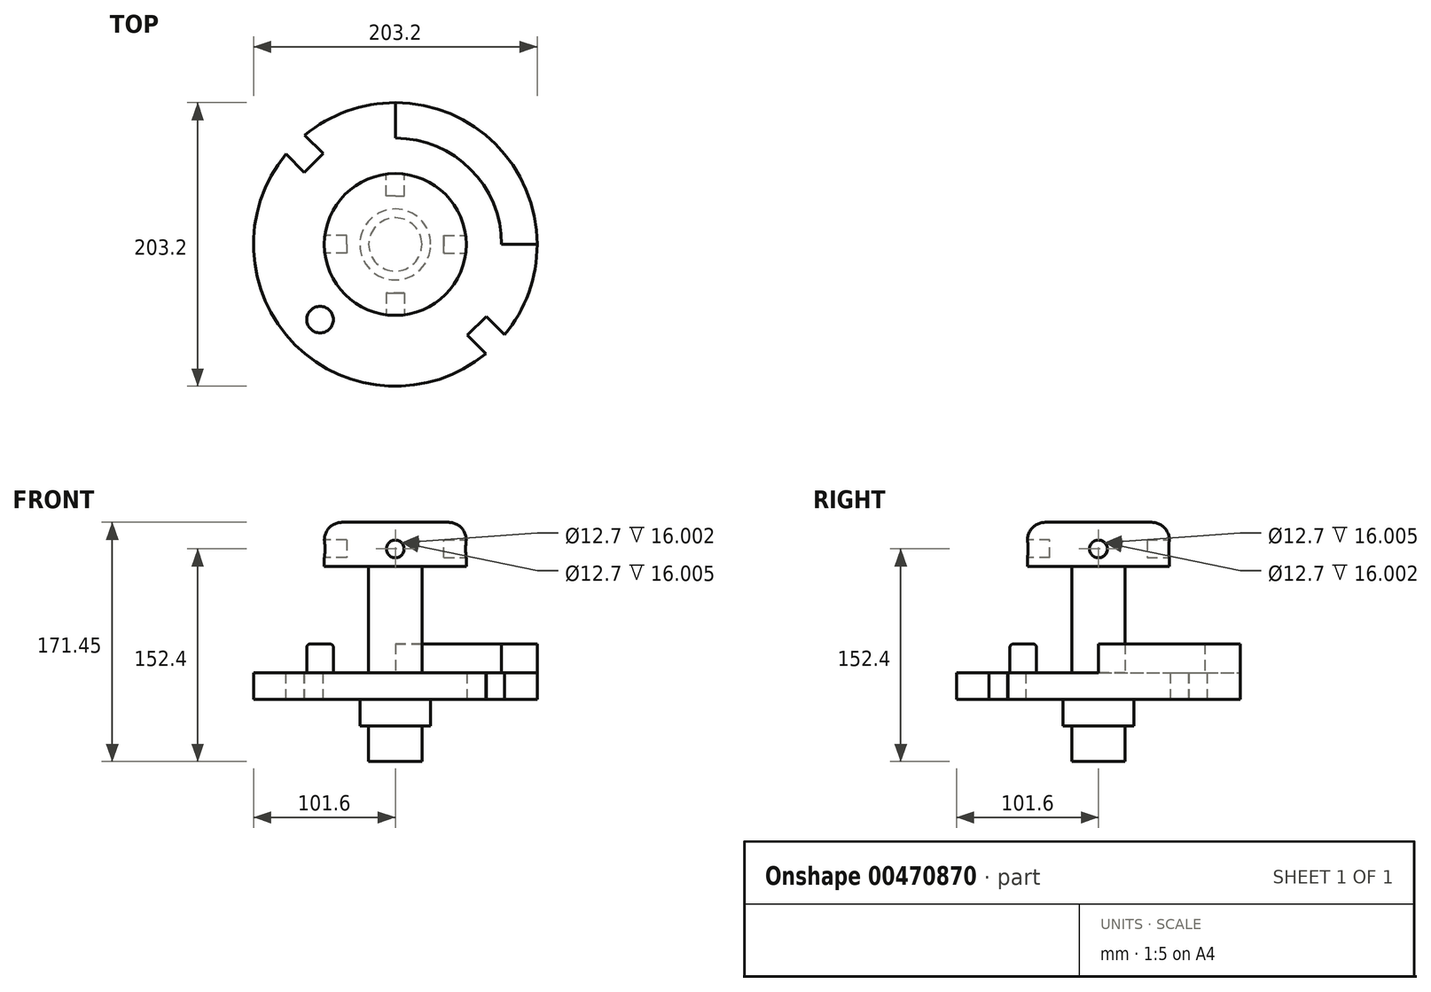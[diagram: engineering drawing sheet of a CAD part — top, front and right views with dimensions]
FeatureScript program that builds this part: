
annotation { "Feature Type Name" : "Feature", "Feature Type Description" : "" }
export const myFeature = defineFeature(function(context is Context, id is Id, definition is map)
    precondition{}
    {
        {
            var Q0;
            Q0=qCreatedBy(makeId("Top.planeOp"),FACE);
            var sketch = newSketch(context, id + "F0", { "sketchPlane" : qUnion([Q0])});
            skCircle(sketch, "E0", {"center": v(0, 0) * mm, "radius": 19.05 * mm});
            skSolve(sketch);
        }
        {
            var Q0;
            Q0=makeQuery(id+"F0.imprint","IMPRINT",FACE,{"disambiguationData":[TD([[makeQuery(id+"F0.imprint","IMPRINT",EDGE,{"derivedFrom":sQuery(id+"F0.wireOp",EDGE,"E0")}),1.0]])]});
            extrude(context, id + "F1", {"entities" : qUnion([Q0]), "depth" : 76.2 * mm});
        }
        {
            var Q0;
            Q0=makeQuery(id+"F1.opExtrude","CAP_FACE",FACE,{"disambiguationData":[OSD([sQuery(id+"F0.wireOp",EDGE,"E0")])],"isStart":false});
            var sketch = newSketch(context, id + "F2", { "sketchPlane" : qUnion([Q0])});
            skCircle(sketch, "E1", {"center": v(0, 0) * mm, "radius": 50.8 * mm});
            skSolve(sketch);
        }
        {
            var Q0;
            Q0=makeQuery(id+"F2.imprint","IMPRINT",FACE,{"disambiguationData":[TD([[makeQuery(id+"F2.imprint","IMPRINT",EDGE,{"derivedFrom":sQuery(id+"F2.wireOp",EDGE,"E1")}),1.0]])]});
            var Q1;
            Q1=makeQuery(id+"F2.imprint","IMPRINT",FACE,{"disambiguationData":[TD([[makeQuery(id+"F2.imprint","IMPRINT",EDGE,{"derivedFrom":makeQuery(id+"F1.opExtrude","CAP_EDGE",EDGE,{"disambiguationData":[OSD([sQuery(id+"F0.wireOp",EDGE,"E0")])],"isStart":false})}),1.0]])]});
            extrude(context, id + "F3", {"entities" : qUnion([Q0, Q1]), "operationType" : NewBodyOperationType.ADD, "depth" : 31.75 * mm});
        }
        {
            var Q0;
            Q0=makeQuery(id+"F3.opExtrude","CAP_EDGE",EDGE,{"disambiguationData":[OSD([sQuery(id+"F2.wireOp",EDGE,"E1")])],"isStart":false});
            fillet(context, id + "F4", {"entities" : qUnion([Q0]), "radius" : 12.7 * mm, "tangentPropagation" : true, "allowEdgeOverflow" : false});
        }
        {
            var Q0;
            Q0=qCreatedBy(makeId("Front.planeOp"),FACE);
            cPlane(context, id + "F5", {"entities" : qUnion([Q0]), "cplaneType" : CPlaneType.OFFSET, "offset" : 50.8 * mm, "width" : 152.4 * mm, "height" : 152.4 * mm});
        }
        {
            var Q0;
            Q0=qCreatedBy(id+"F5.planeOp",FACE);
            var sketch = newSketch(context, id + "F6", { "sketchPlane" : qUnion([Q0])});
            skLineSegment(sketch, "E2", {"start": v(0, 0) * mm, "end": v(0, 88.9) * mm});
            skCircle(sketch, "E3", {"center": v(0, 88.9) * mm, "radius": 6.35 * mm});
            skSolve(sketch);
        }
        {
            var Q0;
            Q0=makeQuery(id+"F6.imprint","IMPRINT",FACE,{"disambiguationData":[TD([[makeQuery(id+"F6.imprint","IMPRINT",EDGE,{"derivedFrom":sQuery(id+"F6.wireOp",EDGE,"E3")}),1.0]])]});
            extrude(context, id + "F7", {"entities" : qUnion([Q0]), "operationType" : NewBodyOperationType.REMOVE, "oppositeDirection" : true, "depth" : 16 * mm});
        }
        {
            var Q0;
            Q0=qCreatedBy(makeId("Right.planeOp"),FACE);
            cPlane(context, id + "F8", {"entities" : qUnion([Q0]), "cplaneType" : CPlaneType.OFFSET, "offset" : 50.8 * mm, "oppositeDirection" : true, "width" : 152.4 * mm, "height" : 152.4 * mm});
        }
        {
            var Q0;
            Q0=qCreatedBy(id+"F8.planeOp",FACE);
            var sketch = newSketch(context, id + "F9", { "sketchPlane" : qUnion([Q0])});
            skLineSegment(sketch, "E4", {"start": v(0, 0) * mm, "end": v(0, 88.9) * mm});
            skCircle(sketch, "E5", {"center": v(0, 88.9) * mm, "radius": 6.35 * mm});
            skSolve(sketch);
        }
        {
            var Q0;
            Q0=makeQuery(id+"F9.imprint","IMPRINT",FACE,{"disambiguationData":[TD([[makeQuery(id+"F9.imprint","IMPRINT",EDGE,{"derivedFrom":sQuery(id+"F9.wireOp",EDGE,"E5")}),1.0]])]});
            extrude(context, id + "F10", {"entities" : qUnion([Q0]), "operationType" : NewBodyOperationType.REMOVE, "depth" : 16 * mm});
        }
        {
            var Q0;
            Q0=qCreatedBy(makeId("Front.planeOp"),FACE);
            cPlane(context, id + "F11", {"entities" : qUnion([Q0]), "cplaneType" : CPlaneType.OFFSET, "offset" : 50.8 * mm, "oppositeDirection" : true, "width" : 152.4 * mm, "height" : 152.4 * mm});
        }
        {
            var Q0;
            Q0=qCreatedBy(id+"F11.planeOp",FACE);
            var sketch = newSketch(context, id + "F12", { "sketchPlane" : qUnion([Q0])});
            skLineSegment(sketch, "E6", {"start": v(0, 0) * mm, "end": v(0, 88.9) * mm});
            skCircle(sketch, "E7", {"center": v(0, 88.9) * mm, "radius": 6.35 * mm});
            skSolve(sketch);
        }
        {
            var Q0;
            Q0=makeQuery(id+"F12.imprint","IMPRINT",FACE,{"disambiguationData":[TD([[makeQuery(id+"F12.imprint","IMPRINT",EDGE,{"derivedFrom":sQuery(id+"F12.wireOp",EDGE,"E7")}),1.0]])]});
            extrude(context, id + "F13", {"entities" : qUnion([Q0]), "operationType" : NewBodyOperationType.REMOVE, "depth" : 16 * mm});
        }
        {
            var Q0;
            Q0=qCreatedBy(makeId("Right.planeOp"),FACE);
            cPlane(context, id + "F14", {"entities" : qUnion([Q0]), "cplaneType" : CPlaneType.OFFSET, "offset" : 50.8 * mm, "width" : 152.4 * mm, "height" : 152.4 * mm});
        }
        {
            var Q0;
            Q0=qCreatedBy(id+"F14.planeOp",FACE);
            var sketch = newSketch(context, id + "F15", { "sketchPlane" : qUnion([Q0])});
            skLineSegment(sketch, "E8", {"start": v(0, 0) * mm, "end": v(0, 88.9) * mm});
            skCircle(sketch, "E9", {"center": v(0, 88.9) * mm, "radius": 6.35 * mm});
            skSolve(sketch);
        }
        {
            var Q0;
            Q0=makeQuery(id+"F15.imprint","IMPRINT",FACE,{"disambiguationData":[TD([[makeQuery(id+"F15.imprint","IMPRINT",EDGE,{"derivedFrom":sQuery(id+"F15.wireOp",EDGE,"E9")}),1.0]])]});
            extrude(context, id + "F16", {"entities" : qUnion([Q0]), "operationType" : NewBodyOperationType.REMOVE, "oppositeDirection" : true, "depth" : 16 * mm});
        }
        {
            var Q0;
            Q0=makeQuery(id+"F1.opExtrude","CAP_FACE",FACE,{"disambiguationData":[OSD([sQuery(id+"F0.wireOp",EDGE,"E0")])],"isStart":true});
            var sketch = newSketch(context, id + "F17", { "sketchPlane" : qUnion([Q0])});
            skCircle(sketch, "E10", {"center": v(0, 0) * mm, "radius": 101.6 * mm});
            skLineSegment(sketch, "E11", {"start": v(0, 0) * mm, "end": v(101.6, 0) * mm});
            skLineSegment(sketch, "E12", {"start": v(0, 0) * mm, "end": v(0, 101.6) * mm});
            skLineSegment(sketch, "E13", {"start": v(0, 101.6) * mm, "end": v(101.6, 101.6) * mm});
            skLineSegment(sketch, "E14", {"start": v(101.6, 101.6) * mm, "end": v(101.6, 0) * mm});
            skLineSegment(sketch, "E15", {"start": v(0, 0) * mm, "end": v(101.6, 101.6) * mm});
            skLineSegment(sketch, "E16.0", {"start": v(32.14, 18.66) * mm, "end": v(108.34, 94.86) * mm});
            skLineSegment(sketch, "E17.0", {"start": v(18.66, 32.14) * mm, "end": v(94.86, 108.34) * mm});
            skLineSegment(sketch, "E18", {"start": v(71.84, 71.84) * mm, "end": v(58.37, 58.37) * mm});
            skLineSegment(sketch, "E19", {"start": v(58.37, 58.37) * mm, "end": v(51.64, 65.1) * mm});
            skLineSegment(sketch, "E20", {"start": v(58.37, 58.37) * mm, "end": v(65.1, 51.64) * mm});
            skLineSegment(sketch, "E21", {"start": v(0, 0) * mm, "end": v(-101.6, 0) * mm});
            skLineSegment(sketch, "E22", {"start": v(0, 101.6) * mm, "end": v(-101.6, 101.6) * mm});
            skLineSegment(sketch, "E23", {"start": v(-101.6, 101.6) * mm, "end": v(-101.6, 0) * mm});
            skLineSegment(sketch, "E24", {"start": v(0, 0) * mm, "end": v(-101.6, 101.6) * mm});
            skLineSegment(sketch, "E25.MirrorCS", {"start": v(-58.37, -58.37) * mm, "end": v(-65.1, -51.64) * mm});
            skLineSegment(sketch, "E26.MirrorCS", {"start": v(-58.37, -58.37) * mm, "end": v(-51.64, -65.1) * mm});
            skLineSegment(sketch, "E27.MirrorCS", {"start": v(-32.14, -18.66) * mm, "end": v(-108.34, -94.86) * mm});
            skLineSegment(sketch, "E28.MirrorCS", {"start": v(-18.66, -32.14) * mm, "end": v(-94.86, -108.34) * mm});
            skSolve(sketch);
        }
        {
            var Q0;
            {var subQ0=sQuery(id+"F17.wireOp",EDGE,"E19");Q0=makeQuery(id+"F17.imprint","IMPRINT",FACE,{"disambiguationData":[TD([[makeQuery(id+"F17.imprint","IMPRINT",EDGE,{"derivedFrom":subQ0}),1.0]])]});}
            var Q1;
            {var subQ1=sQuery(id+"F17.wireOp",EDGE,"E10");var subQ3=sQuery(id+"F17.wireOp",EDGE,"E24");var subQ4=makeQuery(id+"F17.imprint","INTERSECT",VERTEX,{"derivedFrom":[subQ1,subQ3]});Q1=makeQuery(id+"F17.imprint","IMPRINT",FACE,{"disambiguationData":[TD([[makeQuery(id+"F17.imprint","IMPRINT",EDGE,{"disambiguationData":[TD([[subQ4,1.0]])],"derivedFrom":subQ3}),-1.0]])]});}
            var Q2;
            {var subQ1=sQuery(id+"F17.wireOp",EDGE,"E10");var subQ3=sQuery(id+"F17.wireOp",EDGE,"E24");var subQ4=makeQuery(id+"F17.imprint","INTERSECT",VERTEX,{"derivedFrom":[subQ1,subQ3]});Q2=makeQuery(id+"F17.imprint","IMPRINT",FACE,{"disambiguationData":[TD([[makeQuery(id+"F17.imprint","IMPRINT",EDGE,{"disambiguationData":[TD([[subQ4,1.0]])],"derivedFrom":subQ3}),1.0]])]});}
            var Q3;
            {var subQ12=sQuery(id+"F17.wireOp",EDGE,"E25.MirrorCS");Q3=makeQuery(id+"F17.imprint","IMPRINT",FACE,{"disambiguationData":[TD([[makeQuery(id+"F17.imprint","IMPRINT",EDGE,{"derivedFrom":subQ12}),-1.0]])]});}
            var Q4;
            {var subQ0=sQuery(id+"F17.wireOp",EDGE,"E20");Q4=makeQuery(id+"F17.imprint","IMPRINT",FACE,{"disambiguationData":[TD([[makeQuery(id+"F17.imprint","IMPRINT",EDGE,{"derivedFrom":subQ0}),-1.0]])]});}
            var Q5;
            {var subQ1=sQuery(id+"F17.wireOp",EDGE,"E11");var subQ3=makeQuery(id+"F1.opExtrude","CAP_EDGE",EDGE,{"disambiguationData":[OSD([sQuery(id+"F0.wireOp",EDGE,"E0")])],"isStart":true});var subQ4=makeQuery(id+"F17.imprint","INTERSECT",VERTEX,{"derivedFrom":[subQ3,subQ1]});Q5=makeQuery(id+"F17.imprint","IMPRINT",FACE,{"disambiguationData":[TD([[makeQuery(id+"F17.imprint","IMPRINT",EDGE,{"disambiguationData":[TD([[subQ4,-1.0]])],"derivedFrom":subQ3}),-1.0]])]});}
            var Q6;
            {var subQ1=sQuery(id+"F17.wireOp",EDGE,"E12");var subQ3=makeQuery(id+"F1.opExtrude","CAP_EDGE",EDGE,{"disambiguationData":[OSD([sQuery(id+"F0.wireOp",EDGE,"E0")])],"isStart":true});var subQ4=makeQuery(id+"F17.imprint","INTERSECT",VERTEX,{"derivedFrom":[subQ3,subQ1]});Q6=makeQuery(id+"F17.imprint","IMPRINT",FACE,{"disambiguationData":[TD([[makeQuery(id+"F17.imprint","IMPRINT",EDGE,{"disambiguationData":[TD([[subQ4,-1.0]])],"derivedFrom":subQ3}),-1.0]])]});}
            var Q7;
            {var subQ1=sQuery(id+"F17.wireOp",EDGE,"E11");var subQ3=makeQuery(id+"F1.opExtrude","CAP_EDGE",EDGE,{"disambiguationData":[OSD([sQuery(id+"F0.wireOp",EDGE,"E0")])],"isStart":true});var subQ4=makeQuery(id+"F17.imprint","INTERSECT",VERTEX,{"derivedFrom":[subQ3,subQ1]});Q7=makeQuery(id+"F17.imprint","IMPRINT",FACE,{"disambiguationData":[TD([[makeQuery(id+"F17.imprint","IMPRINT",EDGE,{"disambiguationData":[TD([[subQ4,1.0]])],"derivedFrom":subQ3}),-1.0]])]});}
            var Q8;
            {var subQ1=sQuery(id+"F17.wireOp",EDGE,"E21");var subQ3=makeQuery(id+"F1.opExtrude","CAP_EDGE",EDGE,{"disambiguationData":[OSD([sQuery(id+"F0.wireOp",EDGE,"E0")])],"isStart":true});var subQ4=makeQuery(id+"F17.imprint","INTERSECT",VERTEX,{"derivedFrom":[subQ3,subQ1]});Q8=makeQuery(id+"F17.imprint","IMPRINT",FACE,{"disambiguationData":[TD([[makeQuery(id+"F17.imprint","IMPRINT",EDGE,{"disambiguationData":[TD([[subQ4,-1.0]])],"derivedFrom":subQ3}),-1.0]])]});}
            var Q9;
            {var subQ1=sQuery(id+"F17.wireOp",EDGE,"E12");var subQ3=makeQuery(id+"F1.opExtrude","CAP_EDGE",EDGE,{"disambiguationData":[OSD([sQuery(id+"F0.wireOp",EDGE,"E0")])],"isStart":true});var subQ4=makeQuery(id+"F17.imprint","INTERSECT",VERTEX,{"derivedFrom":[subQ3,subQ1]});Q9=makeQuery(id+"F17.imprint","IMPRINT",FACE,{"disambiguationData":[TD([[makeQuery(id+"F17.imprint","IMPRINT",EDGE,{"disambiguationData":[TD([[subQ4,1.0]])],"derivedFrom":subQ3}),-1.0]])]});}
            extrude(context, id + "F18", {"entities" : qUnion([Q0, Q1, Q2, Q3, Q4, Q5, Q6, Q7, Q8, Q9]), "depth" : 19.05 * mm});
        }
        {
            var Q0;
            Q0=makeQuery(id+"F18.opExtrude","CAP_FACE",FACE,{"disambiguationData":[OSD([sQuery(id+"F17.wireOp",EDGE,"E10"),sQuery(id+"F17.wireOp",EDGE,"E16.0"),sQuery(id+"F17.wireOp",EDGE,"E17.0"),sQuery(id+"F17.wireOp",EDGE,"E19"),sQuery(id+"F17.wireOp",EDGE,"E20"),sQuery(id+"F17.wireOp",EDGE,"E25.MirrorCS"),sQuery(id+"F17.wireOp",EDGE,"E26.MirrorCS"),sQuery(id+"F17.wireOp",EDGE,"E27.MirrorCS"),sQuery(id+"F17.wireOp",EDGE,"E28.MirrorCS")])],"isStart":true});
            var sketch = newSketch(context, id + "F19", { "sketchPlane" : qUnion([Q0])});
            skLineSegment(sketch, "E29", {"start": v(0, 0) * mm, "end": v(0, 101.6) * mm});
            skLineSegment(sketch, "E30", {"start": v(0, 0) * mm, "end": v(101.6, 0) * mm});
            skLineSegment(sketch, "E31", {"start": v(101.6, 0) * mm, "end": v(101.6, 101.6) * mm});
            skLineSegment(sketch, "E32", {"start": v(101.6, 101.6) * mm, "end": v(0, 101.6) * mm});
            skLineSegment(sketch, "E33", {"start": v(0, 0) * mm, "end": v(101.6, 101.6) * mm});
            skCircle(sketch, "E34", {"center": v(0, 0) * mm, "radius": 76.2 * mm});
            skCircle(sketch, "E35", {"center": v(53.88, 53.88) * mm, "radius": 9.53 * mm});
            skLineSegment(sketch, "E36", {"start": v(0, 0) * mm, "end": v(-101.6, 0) * mm});
            skLineSegment(sketch, "E37", {"start": v(-101.6, 0) * mm, "end": v(-101.6, 101.6) * mm});
            skLineSegment(sketch, "E38", {"start": v(-101.6, 101.6) * mm, "end": v(0, 101.6) * mm});
            skLineSegment(sketch, "E39", {"start": v(0, 0) * mm, "end": v(-101.6, 101.6) * mm});
            skCircle(sketch, "E40.MirrorC", {"center": v(-53.88, -53.88) * mm, "radius": 9.53 * mm});
            skSolve(sketch);
        }
        {
            var Q0;
            {var subQ0=sQuery(id+"F19.wireOp",EDGE,"E40.MirrorC");var subQ1=sQuery(id+"F19.wireOp",EDGE,"E34");var subQ2=makeQuery(id+"F19.imprint","INTERSECT",VERTEX,{"disambiguationData":[OD(0.0)],"derivedFrom":[subQ1,subQ0]});Q0=makeQuery(id+"F19.imprint","IMPRINT",FACE,{"disambiguationData":[TD([[makeQuery(id+"F19.imprint","IMPRINT",EDGE,{"disambiguationData":[TD([[subQ2,-1.0]])],"derivedFrom":subQ1}),1.0]])]});}
            var Q1;
            {var subQ0=sQuery(id+"F19.wireOp",EDGE,"E40.MirrorC");var subQ1=sQuery(id+"F19.wireOp",EDGE,"E34");var subQ2=makeQuery(id+"F19.imprint","INTERSECT",VERTEX,{"disambiguationData":[OD(0.0)],"derivedFrom":[subQ1,subQ0]});Q1=makeQuery(id+"F19.imprint","IMPRINT",FACE,{"disambiguationData":[TD([[makeQuery(id+"F19.imprint","IMPRINT",EDGE,{"disambiguationData":[TD([[subQ2,-1.0]])],"derivedFrom":subQ1}),-1.0]])]});}
            var Q2;
            {var subQ0=sQuery(id+"F19.wireOp",EDGE,"E35");var subQ1=sQuery(id+"F19.wireOp",EDGE,"E33");var subQ2=makeQuery(id+"F19.imprint","INTERSECT",VERTEX,{"disambiguationData":[OD(0.0)],"derivedFrom":[subQ1,subQ0]});Q2=makeQuery(id+"F19.imprint","IMPRINT",FACE,{"disambiguationData":[TD([[makeQuery(id+"F19.imprint","IMPRINT",EDGE,{"disambiguationData":[TD([[subQ2,-1.0]])],"derivedFrom":subQ1}),-1.0]])]});}
            var Q3;
            {var subQ0=sQuery(id+"F19.wireOp",EDGE,"E35");var subQ1=sQuery(id+"F19.wireOp",EDGE,"E33");var subQ2=makeQuery(id+"F19.imprint","INTERSECT",VERTEX,{"disambiguationData":[OD(0.0)],"derivedFrom":[subQ1,subQ0]});Q3=makeQuery(id+"F19.imprint","IMPRINT",FACE,{"disambiguationData":[TD([[makeQuery(id+"F19.imprint","IMPRINT",EDGE,{"disambiguationData":[TD([[subQ2,-1.0]])],"derivedFrom":subQ1}),1.0]])]});}
            var Q4;
            {var subQ0=sQuery(id+"F19.wireOp",EDGE,"E34");var subQ1=sQuery(id+"F19.wireOp",EDGE,"E33");var subQ2=makeQuery(id+"F19.imprint","INTERSECT",VERTEX,{"derivedFrom":[subQ1,subQ0]});Q4=makeQuery(id+"F19.imprint","IMPRINT",FACE,{"disambiguationData":[TD([[makeQuery(id+"F19.imprint","IMPRINT",EDGE,{"disambiguationData":[TD([[subQ2,-1.0]])],"derivedFrom":subQ1}),1.0]])]});}
            var Q5;
            {var subQ0=sQuery(id+"F19.wireOp",EDGE,"E34");var subQ1=sQuery(id+"F19.wireOp",EDGE,"E33");var subQ2=makeQuery(id+"F19.imprint","INTERSECT",VERTEX,{"derivedFrom":[subQ1,subQ0]});Q5=makeQuery(id+"F19.imprint","IMPRINT",FACE,{"disambiguationData":[TD([[makeQuery(id+"F19.imprint","IMPRINT",EDGE,{"disambiguationData":[TD([[subQ2,-1.0]])],"derivedFrom":subQ1}),-1.0]])]});}
            extrude(context, id + "F20", {"entities" : qUnion([Q0, Q1, Q2, Q3, Q4, Q5]), "operationType" : NewBodyOperationType.ADD, "depth" : 20.83 * mm});
        }
        {
            var Q0;
            Q0=makeQuery(id+"F20.opExtrude","CAP_EDGE",EDGE,{"disambiguationData":[OSD([sQuery(id+"F19.wireOp",EDGE,"E35")])],"isStart":false});
            var Q1;
            Q1=makeQuery(id+"F20.opExtrude","CAP_FACE",FACE,{"disambiguationData":[OSD([sQuery(id+"F19.wireOp",EDGE,"E40.MirrorC")])],"isStart":false});
            fillet(context, id + "F21", {"entities" : qUnion([Q0, Q1]), "radius" : 2.54 * mm, "tangentPropagation" : true, "allowEdgeOverflow" : false});
        }
        {
            var Q0;
            Q0=makeQuery(id+"F18.opExtrude","CAP_FACE",FACE,{"disambiguationData":[OSD([sQuery(id+"F17.wireOp",EDGE,"E10"),sQuery(id+"F17.wireOp",EDGE,"E16.0"),sQuery(id+"F17.wireOp",EDGE,"E17.0"),sQuery(id+"F17.wireOp",EDGE,"E19"),sQuery(id+"F17.wireOp",EDGE,"E20"),sQuery(id+"F17.wireOp",EDGE,"E25.MirrorCS"),sQuery(id+"F17.wireOp",EDGE,"E26.MirrorCS"),sQuery(id+"F17.wireOp",EDGE,"E27.MirrorCS"),sQuery(id+"F17.wireOp",EDGE,"E28.MirrorCS")])],"isStart":false});
            var sketch = newSketch(context, id + "F22", { "sketchPlane" : qUnion([Q0])});
            skCircle(sketch, "E41", {"center": v(0, 0) * mm, "radius": 25.4 * mm});
            skSolve(sketch);
        }
        {
            var Q0;
            Q0=makeQuery(id+"F22.imprint","IMPRINT",FACE,{"disambiguationData":[TD([[makeQuery(id+"F22.imprint","IMPRINT",EDGE,{"derivedFrom":sQuery(id+"F22.wireOp",EDGE,"E41")}),1.0]])]});
            extrude(context, id + "F23", {"entities" : qUnion([Q0]), "operationType" : NewBodyOperationType.ADD, "depth" : 19.05 * mm});
        }
        {
            var Q0;
            Q0=makeQuery(id+"F23.opExtrude","CAP_FACE",FACE,{"disambiguationData":[OSD([sQuery(id+"F22.wireOp",EDGE,"E41")])],"isStart":false});
            var sketch = newSketch(context, id + "F24", { "sketchPlane" : qUnion([Q0])});
            skCircle(sketch, "E42", {"center": v(0, 0) * mm, "radius": 19.05 * mm});
            skSolve(sketch);
        }
        {
            var Q0;
            Q0=makeQuery(id+"F24.imprint","IMPRINT",FACE,{"disambiguationData":[TD([[makeQuery(id+"F24.imprint","IMPRINT",EDGE,{"derivedFrom":sQuery(id+"F24.wireOp",EDGE,"E42")}),1.0]])]});
            extrude(context, id + "F25", {"entities" : qUnion([Q0]), "operationType" : NewBodyOperationType.ADD, "depth" : 25.4 * mm});
        }
    });
